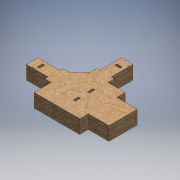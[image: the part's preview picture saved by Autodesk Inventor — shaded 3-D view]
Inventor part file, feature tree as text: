
AUTODESK INVENTOR PART (.ipt)
format: ipt  version: 2016 (Build 200138000, 138)  size: 193,024 bytes
history: native  units: mm
features: extrude x1
ambient origin geometry x8: Origin, YZ Plane, XZ Plane, XY Plane, X Axis, Y Axis, Z Axis, Center Point
bodies: Body1 (feature_tree)
feature tree (1):
  extrude  "Extrusion2"  Depth=1.5mm
